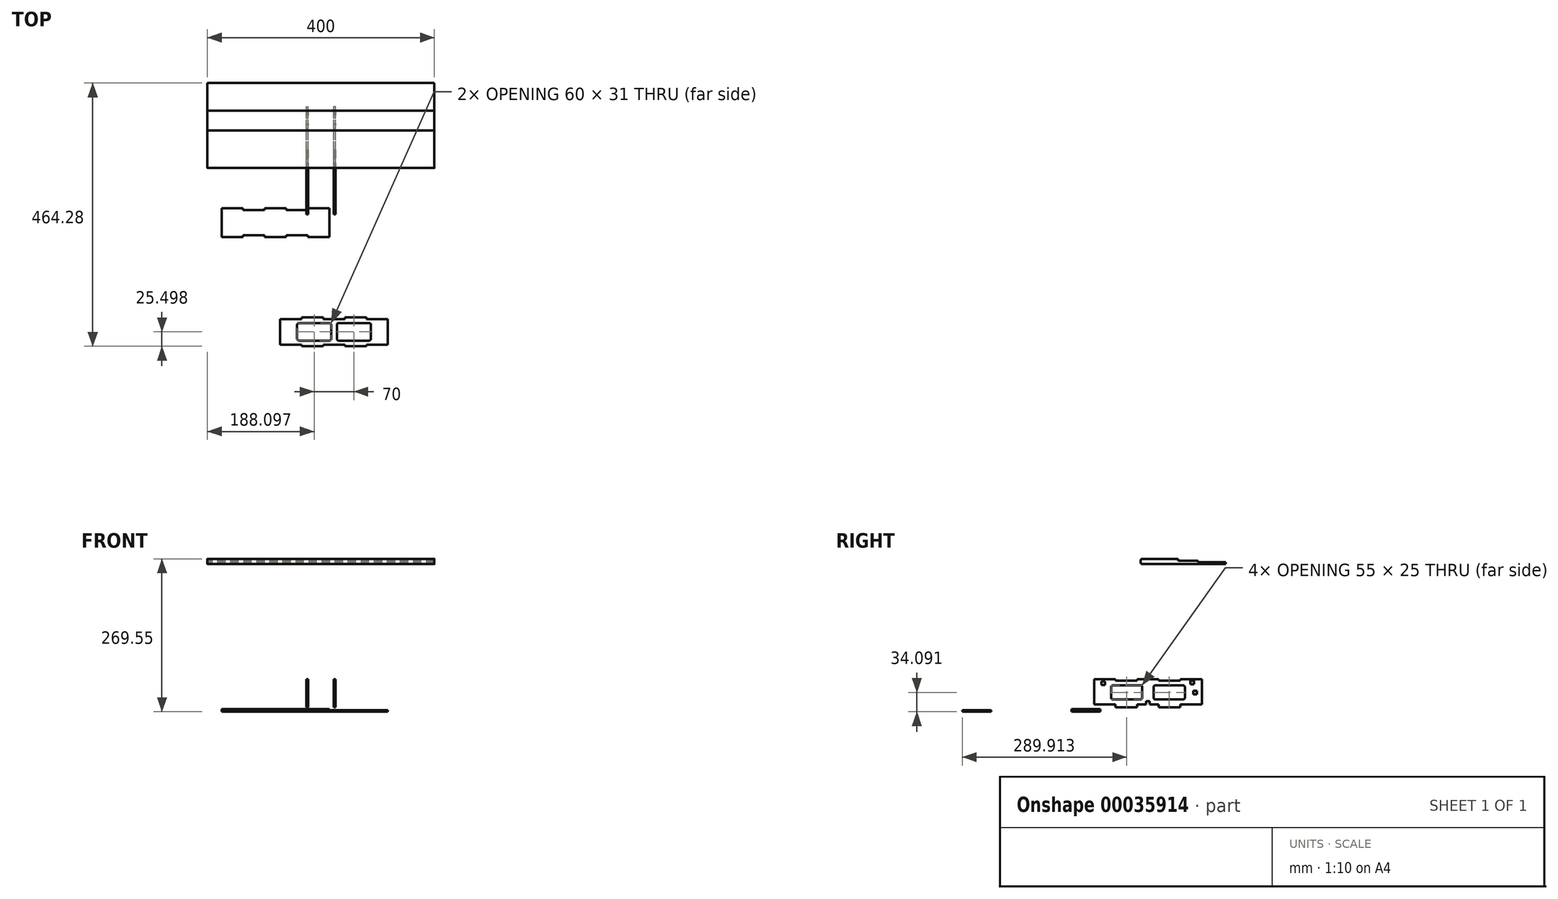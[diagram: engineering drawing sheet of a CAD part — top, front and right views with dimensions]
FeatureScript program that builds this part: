
annotation { "Feature Type Name" : "Feature", "Feature Type Description" : "" }
export const myFeature = defineFeature(function(context is Context, id is Id, definition is map)
    precondition{}
    {
        {
            var Q0;
            Q0=qCreatedBy(makeId("Right.planeOp"),FACE);
            var sketch = newSketch(context, id + "F0", { "sketchPlane" : qUnion([Q0])});
            skLineSegment(sketch, "E0", {"start": v(-91.33, 110.55) * mm, "end": v(55.67, 110.55) * mm});
            skLineSegment(sketch, "E1", {"start": v(55.67, 110.55) * mm, "end": v(55.67, 113.55) * mm});
            skLineSegment(sketch, "E2", {"start": v(55.67, 113.55) * mm, "end": v(6.86, 113.55) * mm});
            skLineSegment(sketch, "E3", {"start": v(6.86, 113.55) * mm, "end": v(6.86, 116.55) * mm});
            skLineSegment(sketch, "E4", {"start": v(6.86, 116.55) * mm, "end": v(-28.06, 116.55) * mm});
            skLineSegment(sketch, "E5", {"start": v(-28.06, 116.55) * mm, "end": v(-28.06, 119.55) * mm});
            skLineSegment(sketch, "E6", {"start": v(-28.06, 119.55) * mm, "end": v(-91.33, 119.55) * mm});
            skLineSegment(sketch, "E7", {"start": v(-94.33, 116.55) * mm, "end": v(-94.33, 113.55) * mm});
            skPoint(sketch, "E8.visualSharp", {"position": v(-94.33, 119.55) * mm});
            skArc(sketch, "E8.filletArc", {"start": v(-91.33, 119.55) * mm, "mid": v(-93.45, 118.67) * mm, "end": v(-94.33, 116.55) * mm});
            skPoint(sketch, "E9.visualSharp", {"position": v(-94.33, 110.55) * mm});
            skArc(sketch, "E9.filletArc", {"start": v(-94.33, 113.55) * mm, "mid": v(-93.45, 111.43) * mm, "end": v(-91.33, 110.55) * mm});
            skSolve(sketch);
        }
        {
            var Q0;
            Q0 = qSketchRegion(id + "F0", true);
            extrude(context, id + "F1", {"entities" : qUnion([Q0]), "endBound" : BoundingType.SYMMETRIC, "depth" : 400 * mm});
        }
        {
            var Q0;
            Q0=qCreatedBy(makeId("Right.planeOp"),FACE);
            cPlane(context, id + "F2", {"entities" : qUnion([Q0]), "cplaneType" : CPlaneType.OFFSET, "offset" : 22.5 * mm, "width" : 150 * mm, "height" : 150 * mm});
        }
        {
            var Q0;
            Q0=qCreatedBy(id+"F2.planeOp",FACE);
            var sketch = newSketch(context, id + "F3", { "sketchPlane" : qUnion([Q0])});
            skLineSegment(sketch, "E10.bottom", {"start": v(-176.2, -92.36) * mm, "end": v(-138.2, -92.36) * mm});
            skLineSegment(sketch, "E10.top", {"start": v(-176.2, -137.36) * mm, "end": v(-138.54, -137.36) * mm});
            skLineSegment(sketch, "E10.left", {"start": v(-176.2, -92.36) * mm, "end": v(-176.2, -137.36) * mm});
            skLineSegment(sketch, "E10.right", {"start": v(13.8, -92.36) * mm, "end": v(13.8, -137.36) * mm});
            skLineSegment(sketch, "E11", {"start": v(-24.2, -92.36) * mm, "end": v(13.8, -92.36) * mm});
            skLineSegment(sketch, "E12", {"start": v(-138.2, -92.36) * mm, "end": v(-138.2, -95.36) * mm});
            skLineSegment(sketch, "E13", {"start": v(-138.2, -95.36) * mm, "end": v(-100.2, -95.36) * mm});
            skLineSegment(sketch, "E14", {"start": v(-100.2, -95.36) * mm, "end": v(-100.2, -92.36) * mm});
            skLineSegment(sketch, "E15", {"start": v(-62.2, -92.36) * mm, "end": v(-62.2, -95.36) * mm});
            skLineSegment(sketch, "E16", {"start": v(-62.2, -95.36) * mm, "end": v(-24.2, -95.36) * mm});
            skLineSegment(sketch, "E17", {"start": v(-24.2, -95.36) * mm, "end": v(-24.2, -92.36) * mm});
            skLineSegment(sketch, "E18", {"start": v(-100.2, -137.36) * mm, "end": v(-84.35, -137.36) * mm});
            skLineSegment(sketch, "E19", {"start": v(-24.2, -137.36) * mm, "end": v(13.8, -137.36) * mm});
            skLineSegment(sketch, "E20", {"start": v(-138.54, -142.06) * mm, "end": v(-138.54, -137.36) * mm});
            skLineSegment(sketch, "E21", {"start": v(-138.54, -142.06) * mm, "end": v(-100.2, -142.06) * mm});
            skLineSegment(sketch, "E22", {"start": v(-100.2, -137.36) * mm, "end": v(-100.2, -142.06) * mm});
            skLineSegment(sketch, "E23", {"start": v(-62.2, -142.06) * mm, "end": v(-62.2, -137.36) * mm});
            skLineSegment(sketch, "E24", {"start": v(-62.2, -142.06) * mm, "end": v(-24.2, -142.06) * mm});
            skLineSegment(sketch, "E25", {"start": v(-24.2, -137.36) * mm, "end": v(-24.2, -142.06) * mm});
            skLineSegment(sketch, "E26.bottom", {"start": v(-163.41, -96.4) * mm, "end": v(-157.06, -96.4) * mm});
            skLineSegment(sketch, "E26.top", {"start": v(-163.41, -102.76) * mm, "end": v(-157.06, -102.76) * mm});
            skLineSegment(sketch, "E26.left", {"start": v(-163.41, -96.4) * mm, "end": v(-163.41, -102.76) * mm});
            skLineSegment(sketch, "E26.right", {"start": v(-157.06, -96.4) * mm, "end": v(-157.06, -102.76) * mm});
            skLineSegment(sketch, "E27.top", {"start": v(-6.2, -101.66) * mm, "end": v(0.1, -101.66) * mm});
            skLineSegment(sketch, "E27.right", {"start": v(0.1, -95.36) * mm, "end": v(0.1, -101.66) * mm});
            skLineSegment(sketch, "E27.left", {"start": v(-6.2, -95.36) * mm, "end": v(-6.2, -101.66) * mm});
            skLineSegment(sketch, "E27.bottom", {"start": v(-6.2, -95.36) * mm, "end": v(0.1, -95.36) * mm});
            skLineSegment(sketch, "E28.bottom", {"start": v(-143.2, -103.4) * mm, "end": v(-94.2, -103.4) * mm});
            skLineSegment(sketch, "E28.top", {"start": v(-143.2, -128.4) * mm, "end": v(-94.2, -128.4) * mm});
            skLineSegment(sketch, "E28.left", {"start": v(-146.2, -106.4) * mm, "end": v(-146.2, -125.4) * mm});
            skLineSegment(sketch, "E28.right", {"start": v(-91.2, -106.4) * mm, "end": v(-91.2, -125.4) * mm});
            skLineSegment(sketch, "E29.bottom", {"start": v(-68.2, -103.4) * mm, "end": v(-19.2, -103.4) * mm});
            skLineSegment(sketch, "E29.top", {"start": v(-68.2, -128.4) * mm, "end": v(-19.2, -128.4) * mm});
            skLineSegment(sketch, "E29.left", {"start": v(-71.2, -106.4) * mm, "end": v(-71.2, -125.4) * mm});
            skLineSegment(sketch, "E29.right", {"start": v(-16.2, -106.4) * mm, "end": v(-16.2, -125.4) * mm});
            skPoint(sketch, "E30.visualSharp", {"position": v(-146.2, -103.4) * mm});
            skArc(sketch, "E30.filletArc", {"start": v(-143.2, -103.4) * mm, "mid": v(-145.32, -104.29) * mm, "end": v(-146.2, -106.4) * mm});
            skPoint(sketch, "E31.visualSharp", {"position": v(-146.2, -128.4) * mm});
            skArc(sketch, "E31.filletArc", {"start": v(-146.2, -125.4) * mm, "mid": v(-145.32, -127.53) * mm, "end": v(-143.2, -128.4) * mm});
            skPoint(sketch, "E32.visualSharp", {"position": v(-91.2, -103.4) * mm});
            skArc(sketch, "E32.filletArc", {"start": v(-91.2, -106.4) * mm, "mid": v(-92.08, -104.29) * mm, "end": v(-94.2, -103.4) * mm});
            skPoint(sketch, "E33.visualSharp", {"position": v(-91.2, -128.4) * mm});
            skArc(sketch, "E33.filletArc", {"start": v(-94.2, -128.4) * mm, "mid": v(-92.08, -127.53) * mm, "end": v(-91.2, -125.4) * mm});
            skPoint(sketch, "E34.visualSharp", {"position": v(-71.2, -103.4) * mm});
            skArc(sketch, "E34.filletArc", {"start": v(-68.2, -103.4) * mm, "mid": v(-70.32, -104.29) * mm, "end": v(-71.2, -106.4) * mm});
            skPoint(sketch, "E35.visualSharp", {"position": v(-71.2, -128.4) * mm});
            skArc(sketch, "E35.filletArc", {"start": v(-71.2, -125.4) * mm, "mid": v(-70.32, -127.53) * mm, "end": v(-68.2, -128.4) * mm});
            skPoint(sketch, "E36.visualSharp", {"position": v(-16.2, -103.4) * mm});
            skArc(sketch, "E36.filletArc", {"start": v(-16.2, -106.4) * mm, "mid": v(-17.08, -104.29) * mm, "end": v(-19.2, -103.4) * mm});
            skPoint(sketch, "E37.visualSharp", {"position": v(-16.2, -128.4) * mm});
            skArc(sketch, "E37.filletArc", {"start": v(-19.2, -128.4) * mm, "mid": v(-17.08, -127.53) * mm, "end": v(-16.2, -125.4) * mm});
            skLineSegment(sketch, "E38", {"start": v(-62.2, -92.36) * mm, "end": v(-100.2, -92.36) * mm});
            skLineSegment(sketch, "E39", {"start": v(-78.05, -137.36) * mm, "end": v(-62.2, -137.36) * mm});
            skLineSegment(sketch, "E40", {"start": v(-84.35, -137.36) * mm, "end": v(-84.35, -131.06) * mm});
            skLineSegment(sketch, "E41", {"start": v(-84.35, -131.06) * mm, "end": v(-78.05, -131.06) * mm});
            skLineSegment(sketch, "E42", {"start": v(-78.05, -131.06) * mm, "end": v(-78.05, -137.36) * mm});
            skLineSegment(sketch, "E43.rect.bottom", {"start": v(4.95, -113.21) * mm, "end": v(-1.35, -113.21) * mm});
            skLineSegment(sketch, "E43.rect.top", {"start": v(4.95, -119.51) * mm, "end": v(-1.35, -119.51) * mm});
            skLineSegment(sketch, "E43.rect.left", {"start": v(4.95, -113.21) * mm, "end": v(4.95, -119.51) * mm});
            skLineSegment(sketch, "E43.rect.right", {"start": v(-1.35, -113.21) * mm, "end": v(-1.35, -119.51) * mm});
            skPoint(sketch, "E43.rect.middle", {"position": v(1.8, -116.36) * mm});
            skPoint(sketch, "E43.rect.middle.positionSnap0", {"position": v(13.8, -114.86) * mm});
            skPoint(sketch, "E43.rect.centerSnap0", {"position": v(13.8, -114.86) * mm});
            skSolve(sketch);
        }
        {
            var Q0;
            Q0 = qSketchRegion(id + "F3", true);
            extrude(context, id + "F4", {"entities" : qUnion([Q0]), "depth" : 3 * mm});
        }
        {
            var Q0;
            Q0=makeQuery(id+"F4.opExtrude","SWEPT_BODY",BODY,{"disambiguationData":[OSD([sQuery(id+"F3.wireOp",EDGE,"E10.bottom"),sQuery(id+"F3.wireOp",EDGE,"E10.top"),sQuery(id+"F3.wireOp",EDGE,"E10.left"),sQuery(id+"F3.wireOp",EDGE,"E10.right"),sQuery(id+"F3.wireOp",EDGE,"74339ce1-3c50-4443-8fcd-9b3fbda0a4b3"),sQuery(id+"F3.wireOp",EDGE,"E11"),sQuery(id+"F3.wireOp",EDGE,"E12"),sQuery(id+"F3.wireOp",EDGE,"E13"),sQuery(id+"F3.wireOp",EDGE,"E14"),sQuery(id+"F3.wireOp",EDGE,"E15"),sQuery(id+"F3.wireOp",EDGE,"E16"),sQuery(id+"F3.wireOp",EDGE,"E17"),sQuery(id+"F3.wireOp",EDGE,"E18"),sQuery(id+"F3.wireOp",EDGE,"E19"),sQuery(id+"F3.wireOp",EDGE,"E20"),sQuery(id+"F3.wireOp",EDGE,"E21"),sQuery(id+"F3.wireOp",EDGE,"E22"),sQuery(id+"F3.wireOp",EDGE,"E23"),sQuery(id+"F3.wireOp",EDGE,"E24"),sQuery(id+"F3.wireOp",EDGE,"E25")])]});
            var Q1;
            Q1=qCreatedBy(makeId("Right.planeOp"),FACE);
            mirror(context, id + "F5", {"operationType" : NewBodyOperationType.ADD, "entities" : qUnion([Q0]), "mirrorPlane" : qUnion([Q1])});
        }
        {
            var Q0;
            Q0=qCreatedBy(makeId("Top.planeOp"),FACE);
            cPlane(context, id + "F6", {"entities" : qUnion([Q0]), "cplaneType" : CPlaneType.OFFSET, "offset" : 150 * mm, "oppositeDirection" : true, "width" : 150 * mm, "height" : 150 * mm});
        }
        {
            var Q0;
            Q0=qCreatedBy(id+"F6.planeOp",FACE);
            var sketch = newSketch(context, id + "F7", { "sketchPlane" : qUnion([Q0])});
            skLineSegment(sketch, "E44.bottom", {"start": v(-33.14, -406.05) * mm, "end": v(11.86, -406.05) * mm});
            skLineSegment(sketch, "E44.top", {"start": v(-33.14, -216.05) * mm, "end": v(11.86, -216.05) * mm});
            skLineSegment(sketch, "E45", {"start": v(-33.14, -368.05) * mm, "end": v(-33.14, -330.05) * mm});
            skLineSegment(sketch, "E46", {"start": v(-33.14, -292.05) * mm, "end": v(-33.14, -254.05) * mm});
            skLineSegment(sketch, "E47", {"start": v(11.86, -368.05) * mm, "end": v(11.86, -330.05) * mm});
            skLineSegment(sketch, "E48", {"start": v(-33.14, -406.05) * mm, "end": v(-36.14, -406.05) * mm});
            skLineSegment(sketch, "E49", {"start": v(-36.14, -406.05) * mm, "end": v(-36.14, -368.05) * mm});
            skLineSegment(sketch, "E50", {"start": v(-36.14, -368.05) * mm, "end": v(-33.14, -368.05) * mm});
            skLineSegment(sketch, "E51", {"start": v(-33.14, -330.05) * mm, "end": v(-36.14, -330.05) * mm});
            skLineSegment(sketch, "E52", {"start": v(-36.14, -330.05) * mm, "end": v(-36.14, -292.05) * mm});
            skLineSegment(sketch, "E53", {"start": v(-36.14, -292.05) * mm, "end": v(-33.14, -292.05) * mm});
            skLineSegment(sketch, "E54", {"start": v(-33.14, -254.05) * mm, "end": v(-36.14, -254.05) * mm});
            skLineSegment(sketch, "E55", {"start": v(-36.14, -254.05) * mm, "end": v(-36.14, -216.05) * mm});
            skLineSegment(sketch, "E56", {"start": v(-36.14, -216.05) * mm, "end": v(-33.14, -216.05) * mm});
            skLineSegment(sketch, "E57", {"start": v(11.86, -216.05) * mm, "end": v(14.86, -216.05) * mm});
            skLineSegment(sketch, "E58", {"start": v(14.86, -216.05) * mm, "end": v(14.86, -254.05) * mm});
            skLineSegment(sketch, "E59", {"start": v(14.86, -292.05) * mm, "end": v(14.86, -330.05) * mm});
            skLineSegment(sketch, "E60", {"start": v(14.86, -330.05) * mm, "end": v(11.86, -330.05) * mm});
            skLineSegment(sketch, "E61", {"start": v(11.86, -368.05) * mm, "end": v(14.86, -368.05) * mm});
            skLineSegment(sketch, "E62", {"start": v(14.86, -368.05) * mm, "end": v(14.86, -406.05) * mm});
            skLineSegment(sketch, "E63", {"start": v(14.86, -406.05) * mm, "end": v(11.86, -406.05) * mm});
            skLineSegment(sketch, "E64", {"start": v(14.86, -292.05) * mm, "end": v(11.86, -292.05) * mm});
            skLineSegment(sketch, "E65", {"start": v(11.86, -292.05) * mm, "end": v(11.86, -254.05) * mm});
            skLineSegment(sketch, "E66", {"start": v(11.86, -254.05) * mm, "end": v(14.86, -254.05) * mm});
            skSolve(sketch);
        }
        {
            var Q0;
            Q0 = qSketchRegion(id + "F7", true);
            extrude(context, id + "F8", {"entities" : qUnion([Q0]), "depth" : 4.7 * mm});
        }
        {
            var Q0;
            Q0=qCreatedBy(id+"F6.planeOp",FACE);
            var sketch = newSketch(context, id + "F9", { "sketchPlane" : qUnion([Q0])});
            skLineSegment(sketch, "E67.bottom", {"start": v(-116.9, -405.61) * mm, "end": v(-71.9, -405.61) * mm});
            skLineSegment(sketch, "E67.top", {"start": v(-116.9, -215.61) * mm, "end": v(-71.9, -215.61) * mm});
            skLineSegment(sketch, "E68", {"start": v(-119.9, -367.61) * mm, "end": v(-116.9, -367.61) * mm});
            skLineSegment(sketch, "E69", {"start": v(-116.9, -329.61) * mm, "end": v(-119.9, -329.61) * mm});
            skLineSegment(sketch, "E70", {"start": v(-119.9, -291.61) * mm, "end": v(-116.9, -291.61) * mm});
            skLineSegment(sketch, "E71", {"start": v(-116.9, -253.61) * mm, "end": v(-119.9, -253.61) * mm});
            skLineSegment(sketch, "E72", {"start": v(-68.9, -329.61) * mm, "end": v(-71.9, -329.61) * mm});
            skLineSegment(sketch, "E73", {"start": v(-71.9, -367.61) * mm, "end": v(-68.9, -367.61) * mm});
            skLineSegment(sketch, "E74", {"start": v(-68.9, -291.61) * mm, "end": v(-71.9, -291.61) * mm});
            skLineSegment(sketch, "E75", {"start": v(-71.9, -253.61) * mm, "end": v(-68.9, -253.61) * mm});
            skLineSegment(sketch, "E76", {"start": v(-116.9, -405.61) * mm, "end": v(-116.9, -367.61) * mm});
            skLineSegment(sketch, "E77", {"start": v(-71.9, -367.61) * mm, "end": v(-71.9, -405.61) * mm});
            skLineSegment(sketch, "E78", {"start": v(-119.9, -367.61) * mm, "end": v(-119.9, -329.61) * mm});
            skLineSegment(sketch, "E79", {"start": v(-68.9, -367.61) * mm, "end": v(-68.9, -329.61) * mm});
            skLineSegment(sketch, "E80", {"start": v(-116.9, -329.61) * mm, "end": v(-116.9, -291.61) * mm});
            skLineSegment(sketch, "E81", {"start": v(-71.9, -329.61) * mm, "end": v(-71.9, -291.61) * mm});
            skLineSegment(sketch, "E82", {"start": v(-68.9, -291.61) * mm, "end": v(-68.9, -253.61) * mm});
            skLineSegment(sketch, "E83", {"start": v(-119.9, -253.61) * mm, "end": v(-119.9, -291.61) * mm});
            skLineSegment(sketch, "E84", {"start": v(-116.9, -253.61) * mm, "end": v(-116.9, -215.61) * mm});
            skLineSegment(sketch, "E85", {"start": v(-71.9, -215.61) * mm, "end": v(-71.9, -253.61) * mm});
            skPoint(sketch, "E86.rect.middle.positionSnap0", {"position": v(-94.4, -215.61) * mm});
            skPoint(sketch, "E86.rect.centerSnap0", {"position": v(-94.4, -215.61) * mm});
            skLineSegment(sketch, "E87.bottom", {"start": v(-106.9, -375.61) * mm, "end": v(-81.9, -375.61) * mm});
            skLineSegment(sketch, "E87.top", {"start": v(-106.9, -315.61) * mm, "end": v(-81.9, -315.61) * mm});
            skLineSegment(sketch, "E87.left", {"start": v(-109.9, -372.61) * mm, "end": v(-109.9, -318.61) * mm});
            skLineSegment(sketch, "E87.right", {"start": v(-78.9, -372.61) * mm, "end": v(-78.9, -318.61) * mm});
            skLineSegment(sketch, "E88.bottom", {"start": v(-106.9, -305.61) * mm, "end": v(-81.9, -305.61) * mm});
            skLineSegment(sketch, "E88.top", {"start": v(-106.9, -245.61) * mm, "end": v(-81.9, -245.61) * mm});
            skLineSegment(sketch, "E88.left", {"start": v(-109.9, -302.61) * mm, "end": v(-109.9, -248.61) * mm});
            skLineSegment(sketch, "E88.right", {"start": v(-78.9, -302.61) * mm, "end": v(-78.9, -248.61) * mm});
            skPoint(sketch, "E89.visualSharp", {"position": v(-109.9, -375.61) * mm});
            skArc(sketch, "E89.filletArc", {"start": v(-109.9, -372.61) * mm, "mid": v(-109.02, -374.73) * mm, "end": v(-106.9, -375.61) * mm});
            skPoint(sketch, "E90.visualSharp", {"position": v(-78.9, -375.61) * mm});
            skArc(sketch, "E90.filletArc", {"start": v(-81.9, -375.61) * mm, "mid": v(-79.78, -374.73) * mm, "end": v(-78.9, -372.61) * mm});
            skPoint(sketch, "E91.visualSharp", {"position": v(-109.9, -315.61) * mm});
            skArc(sketch, "E91.filletArc", {"start": v(-106.9, -315.61) * mm, "mid": v(-109.02, -316.5) * mm, "end": v(-109.9, -318.61) * mm});
            skPoint(sketch, "E92.visualSharp", {"position": v(-78.9, -315.61) * mm});
            skArc(sketch, "E92.filletArc", {"start": v(-78.9, -318.61) * mm, "mid": v(-79.78, -316.5) * mm, "end": v(-81.9, -315.61) * mm});
            skPoint(sketch, "E93.visualSharp", {"position": v(-78.9, -305.61) * mm});
            skArc(sketch, "E93.filletArc", {"start": v(-81.9, -305.61) * mm, "mid": v(-79.78, -304.73) * mm, "end": v(-78.9, -302.61) * mm});
            skPoint(sketch, "E94.visualSharp", {"position": v(-109.9, -305.61) * mm});
            skArc(sketch, "E94.filletArc", {"start": v(-109.9, -302.61) * mm, "mid": v(-109.02, -304.73) * mm, "end": v(-106.9, -305.61) * mm});
            skPoint(sketch, "E95.visualSharp", {"position": v(-109.9, -245.61) * mm});
            skArc(sketch, "E95.filletArc", {"start": v(-106.9, -245.61) * mm, "mid": v(-109.02, -246.5) * mm, "end": v(-109.9, -248.61) * mm});
            skPoint(sketch, "E96.visualSharp", {"position": v(-78.9, -245.61) * mm});
            skArc(sketch, "E96.filletArc", {"start": v(-78.9, -248.61) * mm, "mid": v(-79.78, -246.5) * mm, "end": v(-81.9, -245.61) * mm});
            skSolve(sketch);
        }
        {
            var Q0;
            Q0=makeQuery(id+"F9.imprint","IMPRINT",FACE,{"disambiguationData":[TD([[makeQuery(id+"F9.imprint","IMPRINT",EDGE,{"derivedFrom":sQuery(id+"F9.wireOp",EDGE,"E67.bottom")}),1.0]])]});
            extrude(context, id + "F10", {"entities" : qUnion([Q0]), "depth" : 3 * mm});
        }
        {
            var Q0;
            Q0=makeQuery(id+"F8.opExtrude","SWEPT_BODY",BODY,{"disambiguationData":[OSD([sQuery(id+"F7.wireOp",EDGE,"E44.bottom"),sQuery(id+"F7.wireOp",EDGE,"E44.top"),sQuery(id+"F7.wireOp",EDGE,"E45"),sQuery(id+"F7.wireOp",EDGE,"E46"),sQuery(id+"F7.wireOp",EDGE,"E47"),sQuery(id+"F7.wireOp",EDGE,"E48"),sQuery(id+"F7.wireOp",EDGE,"E49"),sQuery(id+"F7.wireOp",EDGE,"E50"),sQuery(id+"F7.wireOp",EDGE,"E51"),sQuery(id+"F7.wireOp",EDGE,"E52"),sQuery(id+"F7.wireOp",EDGE,"E53"),sQuery(id+"F7.wireOp",EDGE,"E54"),sQuery(id+"F7.wireOp",EDGE,"E55"),sQuery(id+"F7.wireOp",EDGE,"E56"),sQuery(id+"F7.wireOp",EDGE,"E57"),sQuery(id+"F7.wireOp",EDGE,"E58"),sQuery(id+"F7.wireOp",EDGE,"E59"),sQuery(id+"F7.wireOp",EDGE,"E60"),sQuery(id+"F7.wireOp",EDGE,"E61"),sQuery(id+"F7.wireOp",EDGE,"E62"),sQuery(id+"F7.wireOp",EDGE,"E63"),sQuery(id+"F7.wireOp",EDGE,"E64"),sQuery(id+"F7.wireOp",EDGE,"E65"),sQuery(id+"F7.wireOp",EDGE,"E66")])]});
            var Q1;
            Q1=makeQuery(id+"F8.opExtrude","SWEPT_EDGE",EDGE,{"disambiguationData":[OSD([sQuery(id+"F7.wireOp",EDGE,"E57"),sQuery(id+"F7.wireOp",EDGE,"E58")])]});
            transform(context, id + "F11", {"entities" : qUnion([Q0]), "transformType" : TransformType.ROTATION, "transformAxis" : qUnion([Q1]), "angle" : 90 * degree, "makeCopy" : false});
        }
        {
            var Q0;
            Q0=makeQuery(id+"F10.opExtrude","SWEPT_BODY",BODY,{"disambiguationData":[OSD([sQuery(id+"F9.wireOp",EDGE,"E67.bottom"),sQuery(id+"F9.wireOp",EDGE,"E67.top"),sQuery(id+"F9.wireOp",EDGE,"E68"),sQuery(id+"F9.wireOp",EDGE,"E69"),sQuery(id+"F9.wireOp",EDGE,"E70"),sQuery(id+"F9.wireOp",EDGE,"E71"),sQuery(id+"F9.wireOp",EDGE,"E72"),sQuery(id+"F9.wireOp",EDGE,"E73"),sQuery(id+"F9.wireOp",EDGE,"E74"),sQuery(id+"F9.wireOp",EDGE,"E75"),sQuery(id+"F9.wireOp",EDGE,"E76"),sQuery(id+"F9.wireOp",EDGE,"E77"),sQuery(id+"F9.wireOp",EDGE,"E78"),sQuery(id+"F9.wireOp",EDGE,"E79"),sQuery(id+"F9.wireOp",EDGE,"E80"),sQuery(id+"F9.wireOp",EDGE,"E81"),sQuery(id+"F9.wireOp",EDGE,"E82"),sQuery(id+"F9.wireOp",EDGE,"E83"),sQuery(id+"F9.wireOp",EDGE,"E84"),sQuery(id+"F9.wireOp",EDGE,"E85"),sQuery(id+"F9.wireOp",EDGE,"E86.rect.bottom"),sQuery(id+"F9.wireOp",EDGE,"E86.rect.top"),sQuery(id+"F9.wireOp",EDGE,"E86.rect.left"),sQuery(id+"F9.wireOp",EDGE,"E86.rect.right"),sQuery(id+"F9.wireOp",EDGE,"f572d935-fe0c-44f3-9332-d38376464846.filletArc"),sQuery(id+"F9.wireOp",EDGE,"378187a6-a5d3-4038-aba9-e9b447b0166c.filletArc"),sQuery(id+"F9.wireOp",EDGE,"9679ccf6-e979-4820-aa32-bc166837eb4f.filletArc"),sQuery(id+"F9.wireOp",EDGE,"ae985213-cf9b-42a1-a693-2ca5755f400f.filletArc")])]});
            var Q1;
            Q1=makeQuery(id+"F10.opExtrude","SWEPT_EDGE",EDGE,{"disambiguationData":[OSD([sQuery(id+"F9.wireOp",EDGE,"E67.bottom"),sQuery(id+"F9.wireOp",EDGE,"E77")])]});
            transform(context, id + "F12", {"entities" : qUnion([Q0]), "transformType" : TransformType.ROTATION, "transformAxis" : qUnion([Q1]), "angle" : 90 * degree, "makeCopy" : false});
        }
    });
